# Revit family: STE14
name_source: partatom
category: Lighting Fixtures
revit_build: Autodesk Revit Architecture 2012 (Build: 20110309_2315(x64)
units: mm (PartAtom-declared; Revit-internal decimal feet)

## types (7) — shared parameters
Backbox = White
Color Filter = 16777215
Default Elevation = 48.000"
Description = 1' × 4' Stratus® Recessed Indirect / 1, 2, or 3-Lamp T5, T5HO, T8
Dimming Lamp Color Temperature Shift = <None>
Emit from Line Length = 46.000"
Glass = Glass
Lamp = 3
Manufacturer = Columbia Lighting
Manufacturer Fax = 866.898.1065
Model = STE14
Product Documentation Link = http://www.columbialighting.com
Product Page URL = http://www.columbialighting.com
Tilt Angle = -90.00°
URL = http://www.columbialighting.com
Wattage Comments = 71W

## per-type parameters (varying)
| type | Photometric Web File |
| STE14-154G-MPO-EPU | 3875.IES |
| STE14-228G-MPO-EPU | 3879.IES |
| STE14-232G-MPO-EU | 3849.IES |
| STE14-254G-MPO-EPU | 3873.IES |
| STE14-328G-MPO-EPU | 3881.IES |
| STE14-332G-MPO-3EU | 3847.IES |
| STE14-354G-MPO-EPU | 3871.IES |

## geometry (parser evidence)
native form markers: Blend x1, Sweep x1
no freeform markers — native parametric forms only
